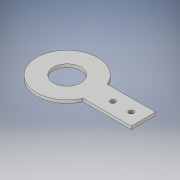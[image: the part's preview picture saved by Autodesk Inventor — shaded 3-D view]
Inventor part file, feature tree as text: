
AUTODESK INVENTOR PART (.ipt)
format: ipt  version: 2018 (Build 220112000, 112)  size: 114,176 bytes
history: native  units: in
note: dims shown in document units (in); Inventor stores cm internally (conversion verified against a paired STEP export)
features: extrude x1, sketch x1
ambient origin geometry x8: Origin, YZ Plane, XZ Plane, XY Plane, X Axis, Y Axis, Z Axis, Center Point
bodies: Solid1 (feature_tree)
feature tree (2):
  extrude  "Extrusion1"  Depth=0.125in
  sketch  "Sketch1"  dims[d0=0.5in d1=2.0in d2=1.125in d3=1.125in d4=2.5in d5=0.5in d6=0.75in d7=0.2031in d8=0.2031in d9=0.125in d10=0.0in]
